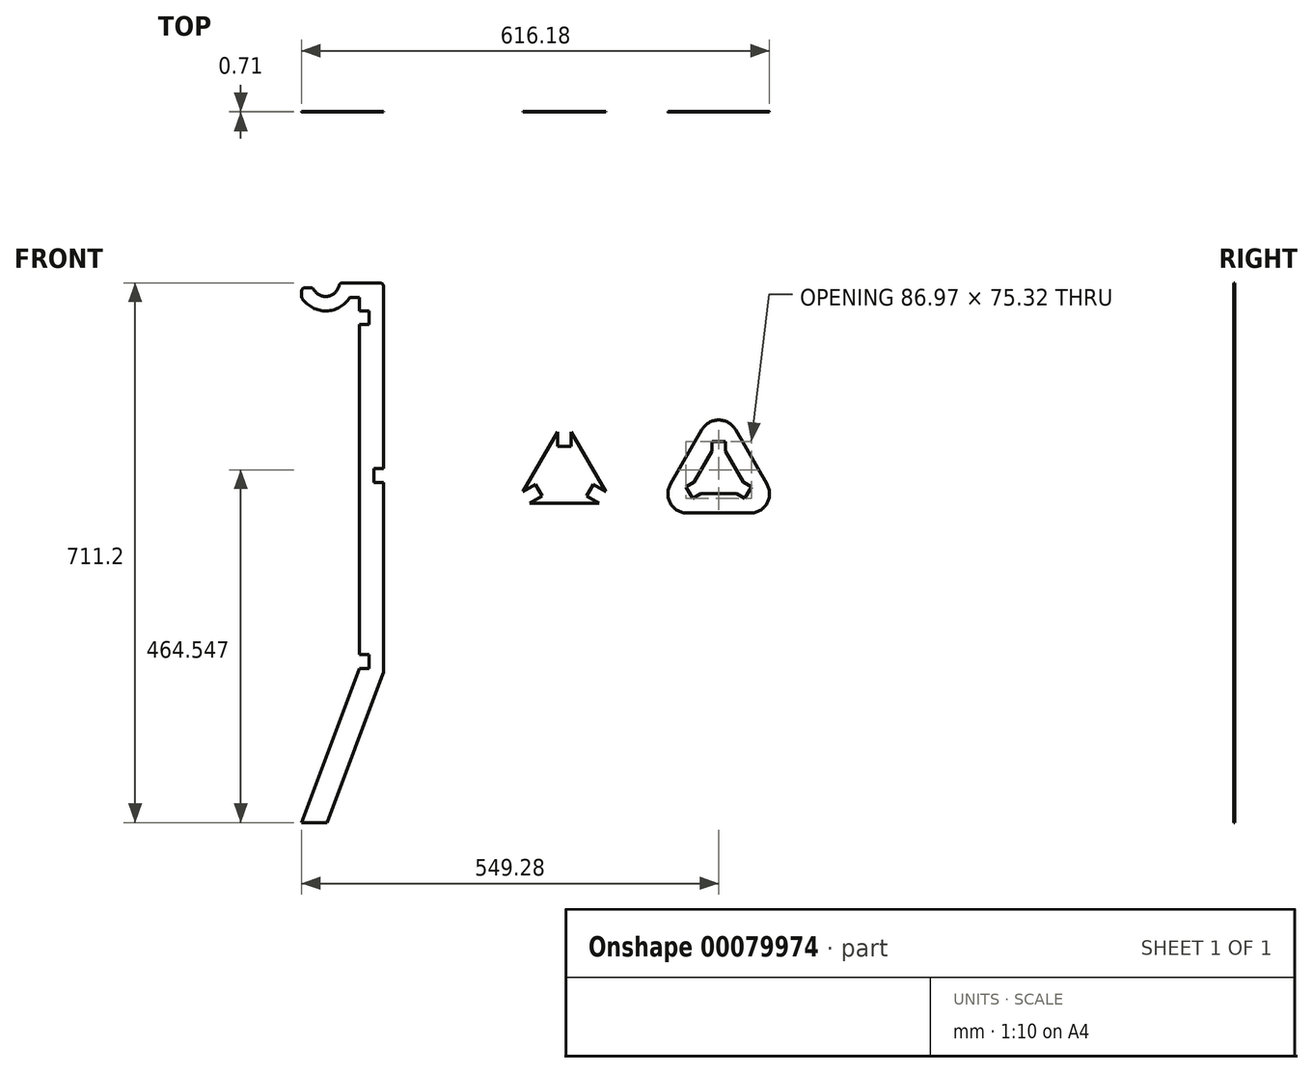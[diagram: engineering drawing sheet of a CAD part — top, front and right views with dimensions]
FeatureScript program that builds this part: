
annotation { "Feature Type Name" : "Feature", "Feature Type Description" : "" }
export const myFeature = defineFeature(function(context is Context, id is Id, definition is map)
    precondition{}
    {
        {
            assignVariable(context, id + "F0", {"name" : "Thickness", "anyValue" : .71});
        }
        {
            var Q0;
            Q0=qCreatedBy(makeId("Front.planeOp"),FACE);
            var sketch = newSketch(context, id + "F1", { "sketchPlane" : qUnion([Q0])});
            skLineSegment(sketch, "E0.bottom", {"start": v(-15.88, 254) * mm, "end": v(15.87, 254) * mm});
            skLineSegment(sketch, "E0.left", {"start": v(-15.88, 254) * mm, "end": v(-15.87, -254) * mm});
            skLineSegment(sketch, "E0.right", {"start": v(15.87, 254) * mm, "end": v(15.88, -259.76) * mm});
            skPoint(sketch, "E0.middle", {"position": v(0, 0) * mm});
            skLineSegment(sketch, "E1", {"start": v(-15.87, -254) * mm, "end": v(-92.07, -457.2) * mm});
            skLineSegment(sketch, "E2.0", {"start": v(15.88, -259.76) * mm, "end": v(-58.17, -457.2) * mm});
            skLineSegment(sketch, "E3", {"start": v(-92.07, -457.2) * mm, "end": v(-58.17, -457.2) * mm});
            skLineSegment(sketch, "E4.bottom", {"start": v(-15.88, 254) * mm, "end": v(-28.58, 254) * mm});
            skLineSegment(sketch, "E4.top", {"start": v(-15.88, 234.95) * mm, "end": v(-28.58, 234.95) * mm});
            skLineSegment(sketch, "E4.left", {"start": v(-15.88, 254) * mm, "end": v(-15.88, 234.95) * mm});
            skLineSegment(sketch, "E4.right", {"start": v(-28.58, 254) * mm, "end": v(-28.58, 234.95) * mm});
            skArc(sketch, "E5", {"start": v(-92.08, 234.95) * mm, "mid": v(-60.33, 216.97) * mm, "end": v(-28.58, 234.95) * mm});
            skArc(sketch, "E6.0", {"start": v(-77.14, 247.65) * mm, "mid": v(-57.1, 236.32) * mm, "end": v(-42.35, 254) * mm});
            skLineSegment(sketch, "E7", {"start": v(-92.08, 234.95) * mm, "end": v(-92.08, 247.65) * mm});
            skLineSegment(sketch, "E8", {"start": v(-92.08, 247.65) * mm, "end": v(-77.14, 247.65) * mm});
            skLineSegment(sketch, "E9", {"start": v(-42.35, 254) * mm, "end": v(-28.58, 254) * mm});
            skLineSegment(sketch, "E10", {"start": v(-15.88, 0) * mm, "end": v(15.88, 0) * mm, "construction": true});
            skPoint(sketch, "E11.firstSnap0", {"position": v(-60.33, 216.97) * mm});
            skLineSegment(sketch, "E11.bottom", {"start": v(-15.88, 216.97) * mm, "end": v(-3.18, 216.97) * mm});
            skLineSegment(sketch, "E11.top", {"start": v(-15.88, 198.94) * mm, "end": v(-3.18, 198.94) * mm});
            skLineSegment(sketch, "E11.left", {"start": v(-15.88, 216.97) * mm, "end": v(-15.88, 198.94) * mm});
            skLineSegment(sketch, "E11.right", {"start": v(-3.18, 216.97) * mm, "end": v(-3.18, 198.94) * mm});
            skLineSegment(sketch, "E12.bottom", {"start": v(-15.87, -254) * mm, "end": v(-3.17, -254) * mm});
            skLineSegment(sketch, "E12.top", {"start": v(-15.87, -235.97) * mm, "end": v(-3.17, -235.97) * mm});
            skLineSegment(sketch, "E12.left", {"start": v(-15.87, -254) * mm, "end": v(-15.87, -235.97) * mm});
            skLineSegment(sketch, "E12.right", {"start": v(-3.17, -254) * mm, "end": v(-3.17, -235.97) * mm});
            skLineSegment(sketch, "E13.bottom", {"start": v(15.88, 0) * mm, "end": v(3.18, 0) * mm, "construction": true});
            skLineSegment(sketch, "E13.top", {"start": v(15.88, 9.02) * mm, "end": v(3.18, 9.02) * mm});
            skLineSegment(sketch, "E13.left", {"start": v(15.88, 0) * mm, "end": v(15.88, 9.02) * mm});
            skLineSegment(sketch, "E13.right", {"start": v(3.18, 0) * mm, "end": v(3.18, 9.02) * mm});
            skLineSegment(sketch, "E14.MirrorCS", {"start": v(3.18, 0) * mm, "end": v(3.18, -9.02) * mm});
            skLineSegment(sketch, "E15.MirrorCS", {"start": v(15.88, -9.02) * mm, "end": v(3.18, -9.02) * mm});
            skCircle(sketch, "E16.cCircle", {"center": v(254, 0) * mm, "radius": 36.66 * mm, "construction": true});
            skLineSegment(sketch, "E16.0", {"start": v(254, 73.32) * mm, "end": v(317.5, -36.66) * mm});
            skLineSegment(sketch, "E16.1", {"start": v(317.5, -36.66) * mm, "end": v(190.5, -36.66) * mm});
            skLineSegment(sketch, "E16.2", {"start": v(190.5, -36.66) * mm, "end": v(254, 73.32) * mm});
            skPoint(sketch, "E16.0.midPoint", {"position": v(285.75, 18.33) * mm});
            skLineSegment(sketch, "E17", {"start": v(244.98, 57.7) * mm, "end": v(263.02, 57.7) * mm, "construction": true});
            skLineSegment(sketch, "E18.top", {"start": v(244.98, 38.66) * mm, "end": v(263.02, 38.66) * mm});
            skLineSegment(sketch, "E18.left", {"start": v(244.98, 57.7) * mm, "end": v(244.98, 38.66) * mm});
            skLineSegment(sketch, "E18.right", {"start": v(263.02, 57.7) * mm, "end": v(263.02, 38.66) * mm});
            skLineSegment(sketch, "E19.1.0", {"start": v(208.53, -36.66) * mm, "end": v(225.03, -27.14) * mm});
            skLineSegment(sketch, "E19.1.1", {"start": v(225.03, -27.14) * mm, "end": v(216.01, -11.52) * mm});
            skLineSegment(sketch, "E19.1.2", {"start": v(199.52, -21.04) * mm, "end": v(216.01, -11.52) * mm});
            skLineSegment(sketch, "E19.2.0", {"start": v(308.48, -21.04) * mm, "end": v(291.99, -11.52) * mm});
            skLineSegment(sketch, "E19.2.1", {"start": v(291.99, -11.52) * mm, "end": v(282.97, -27.14) * mm});
            skLineSegment(sketch, "E19.2.2", {"start": v(299.47, -36.66) * mm, "end": v(282.97, -27.14) * mm});
            skCircle(sketch, "E20.cCircle", {"center": v(457.2, 0) * mm, "radius": 36.66 * mm, "construction": true});
            skLineSegment(sketch, "E20.0", {"start": v(457.2, 73.32) * mm, "end": v(520.7, -36.66) * mm, "construction": true});
            skLineSegment(sketch, "E20.1", {"start": v(520.7, -36.66) * mm, "end": v(393.7, -36.66) * mm, "construction": true});
            skLineSegment(sketch, "E20.2", {"start": v(393.7, -36.66) * mm, "end": v(457.2, 73.32) * mm, "construction": true});
            skPoint(sketch, "E20.0.midPoint", {"position": v(488.95, 18.33) * mm});
            skLineSegment(sketch, "E21", {"start": v(448.18, 57.7) * mm, "end": v(466.22, 57.7) * mm, "construction": true});
            skLineSegment(sketch, "E22.top", {"start": v(448.18, 38.66) * mm, "end": v(466.22, 38.66) * mm, "construction": true});
            skLineSegment(sketch, "E22.left", {"start": v(448.18, 57.7) * mm, "end": v(448.18, 38.66) * mm, "construction": true});
            skLineSegment(sketch, "E22.right", {"start": v(466.22, 57.7) * mm, "end": v(466.22, 38.66) * mm, "construction": true});
            skLineSegment(sketch, "E23.1.0", {"start": v(411.73, -36.66) * mm, "end": v(428.23, -27.14) * mm, "construction": true});
            skLineSegment(sketch, "E23.1.1", {"start": v(428.23, -27.14) * mm, "end": v(419.21, -11.52) * mm, "construction": true});
            skLineSegment(sketch, "E23.1.2", {"start": v(402.72, -21.04) * mm, "end": v(419.21, -11.52) * mm, "construction": true});
            skLineSegment(sketch, "E23.2.0", {"start": v(511.68, -21.04) * mm, "end": v(495.19, -11.52) * mm, "construction": true});
            skLineSegment(sketch, "E23.2.1", {"start": v(495.19, -11.52) * mm, "end": v(486.17, -27.14) * mm, "construction": true});
            skLineSegment(sketch, "E23.2.2", {"start": v(502.67, -36.66) * mm, "end": v(486.17, -27.14) * mm, "construction": true});
            skLineSegment(sketch, "E24.bottom", {"start": v(448.18, 45) * mm, "end": v(466.22, 45) * mm});
            skLineSegment(sketch, "E24.top", {"start": v(448.18, 32.3) * mm, "end": v(466.22, 32.3) * mm});
            skLineSegment(sketch, "E24.left", {"start": v(448.18, 45) * mm, "end": v(448.18, 32.3) * mm});
            skLineSegment(sketch, "E24.right", {"start": v(466.22, 45) * mm, "end": v(466.22, 32.3) * mm});
            skLineSegment(sketch, "E25.1.0", {"start": v(422.73, -30.31) * mm, "end": v(433.73, -23.96) * mm});
            skLineSegment(sketch, "E25.1.1", {"start": v(422.73, -30.31) * mm, "end": v(413.72, -14.7) * mm});
            skLineSegment(sketch, "E25.1.2", {"start": v(413.72, -14.7) * mm, "end": v(424.71, -8.34) * mm});
            skLineSegment(sketch, "E25.1.3", {"start": v(433.73, -23.96) * mm, "end": v(424.71, -8.34) * mm});
            skLineSegment(sketch, "E25.2.0", {"start": v(500.68, -14.7) * mm, "end": v(489.69, -8.34) * mm});
            skLineSegment(sketch, "E25.2.1", {"start": v(500.68, -14.7) * mm, "end": v(491.67, -30.31) * mm});
            skLineSegment(sketch, "E25.2.2", {"start": v(491.67, -30.31) * mm, "end": v(480.67, -23.96) * mm});
            skLineSegment(sketch, "E25.2.3", {"start": v(489.69, -8.34) * mm, "end": v(480.67, -23.96) * mm});
            skLineSegment(sketch, "E26", {"start": v(466.22, 32.3) * mm, "end": v(489.69, -8.34) * mm});
            skLineSegment(sketch, "E27", {"start": v(433.73, -23.96) * mm, "end": v(480.67, -23.96) * mm});
            skLineSegment(sketch, "E28", {"start": v(424.71, -8.34) * mm, "end": v(448.18, 32.3) * mm});
            skLineSegment(sketch, "E29.0", {"start": v(371.7, -49.36) * mm, "end": v(457.2, 98.72) * mm});
            skLineSegment(sketch, "E30.0", {"start": v(457.2, 98.72) * mm, "end": v(542.7, -49.36) * mm});
            skLineSegment(sketch, "E31.0", {"start": v(371.7, -49.36) * mm, "end": v(542.7, -49.36) * mm});
            skSolve(sketch);
        }
        {
            var Q0;
            Q0=makeQuery(id+"F1.imprint","IMPRINT",FACE,{"disambiguationData":[TD([[makeQuery(id+"F1.imprint","IMPRINT",EDGE,{"derivedFrom":sQuery(id+"F1.wireOp",EDGE,"E24.bottom")}),1.0]])]});
            var Q1;
            {var subQ8=sQuery(id+"F1.wireOp",EDGE,"E18.top");Q1=makeQuery(id+"F1.imprint","IMPRINT",FACE,{"disambiguationData":[TD([[makeQuery(id+"F1.imprint","IMPRINT",EDGE,{"derivedFrom":subQ8}),-1.0]])]});}
            var Q2;
            {var subQ3=sQuery(id+"F1.wireOp",EDGE,"E0.bottom");Q2=makeQuery(id+"F1.imprint","IMPRINT",FACE,{"disambiguationData":[TD([[makeQuery(id+"F1.imprint","IMPRINT",EDGE,{"derivedFrom":subQ3}),-1.0]])]});}
            var Q3;
            Q3=makeQuery(id+"F1.imprint","IMPRINT",FACE,{"disambiguationData":[TD([[makeQuery(id+"F1.imprint","IMPRINT",EDGE,{"derivedFrom":sQuery(id+"F1.wireOp",EDGE,"E4.bottom")}),1.0]])]});
            var Q4;
            Q4=makeQuery(id+"F1.imprint","IMPRINT",FACE,{"disambiguationData":[TD([[makeQuery(id+"F1.imprint","IMPRINT",EDGE,{"derivedFrom":sQuery(id+"F1.wireOp",EDGE,"E4.right")}),-1.0]])]});
            extrude(context, id + "F2", {"entities" : qUnion([Q0, Q1, Q2, Q3, Q4]), "depth" : (getVariable(context, 'Thickness')) * mm});
        }
        {
            var Q0;
            Q0=makeQuery(id+"F2.opExtrude","SWEPT_EDGE",EDGE,{"disambiguationData":[OSD([sQuery(id+"F1.wireOp",EDGE,"E29.0"),sQuery(id+"F1.wireOp",EDGE,"E30.0")])]});
            var Q1;
            Q1=makeQuery(id+"F2.opExtrude","SWEPT_EDGE",EDGE,{"disambiguationData":[OSD([sQuery(id+"F1.wireOp",EDGE,"E30.0"),sQuery(id+"F1.wireOp",EDGE,"E31.0")])]});
            var Q2;
            Q2=makeQuery(id+"F2.opExtrude","SWEPT_EDGE",EDGE,{"disambiguationData":[OSD([sQuery(id+"F1.wireOp",EDGE,"E29.0"),sQuery(id+"F1.wireOp",EDGE,"E31.0")])]});
            fillet(context, id + "F3", {"entities" : qUnion([Q0, Q1, Q2]), "radius" : 25.4 * mm, "tangentPropagation" : true, "allowEdgeOverflow" : false});
        }
        {
            var Q0;
            Q0=makeQuery(id+"F2.opExtrude","SWEPT_EDGE",EDGE,{"disambiguationData":[OSD([sQuery(id+"F1.wireOp",EDGE,"E0.right"),sQuery(id+"F1.wireOp",EDGE,"E2.0")])]});
            var Q1;
            Q1=makeQuery(id+"F2.opExtrude","SWEPT_EDGE",EDGE,{"disambiguationData":[OSD([sQuery(id+"F1.wireOp",EDGE,"E0.bottom"),sQuery(id+"F1.wireOp",EDGE,"E0.right")])]});
            var Q2;
            Q2=makeQuery(id+"F2.opExtrude","SWEPT_EDGE",EDGE,{"disambiguationData":[OSD([sQuery(id+"F1.wireOp",EDGE,"E6.0"),sQuery(id+"F1.wireOp",EDGE,"E9")])]});
            var Q3;
            Q3=makeQuery(id+"F2.opExtrude","SWEPT_EDGE",EDGE,{"disambiguationData":[OSD([sQuery(id+"F1.wireOp",EDGE,"E6.0"),sQuery(id+"F1.wireOp",EDGE,"E8")])]});
            var Q4;
            Q4=makeQuery(id+"F2.opExtrude","SWEPT_EDGE",EDGE,{"disambiguationData":[OSD([sQuery(id+"F1.wireOp",EDGE,"E7"),sQuery(id+"F1.wireOp",EDGE,"E8")])]});
            var Q5;
            Q5=makeQuery(id+"F2.opExtrude","SWEPT_EDGE",EDGE,{"disambiguationData":[OSD([sQuery(id+"F1.wireOp",EDGE,"E5"),sQuery(id+"F1.wireOp",EDGE,"E7")])]});
            fillet(context, id + "F4", {"entities" : qUnion([Q0, Q1, Q2, Q3, Q4, Q5]), "radius" : 5.08 * mm, "tangentPropagation" : true, "allowEdgeOverflow" : false});
        }
    });
